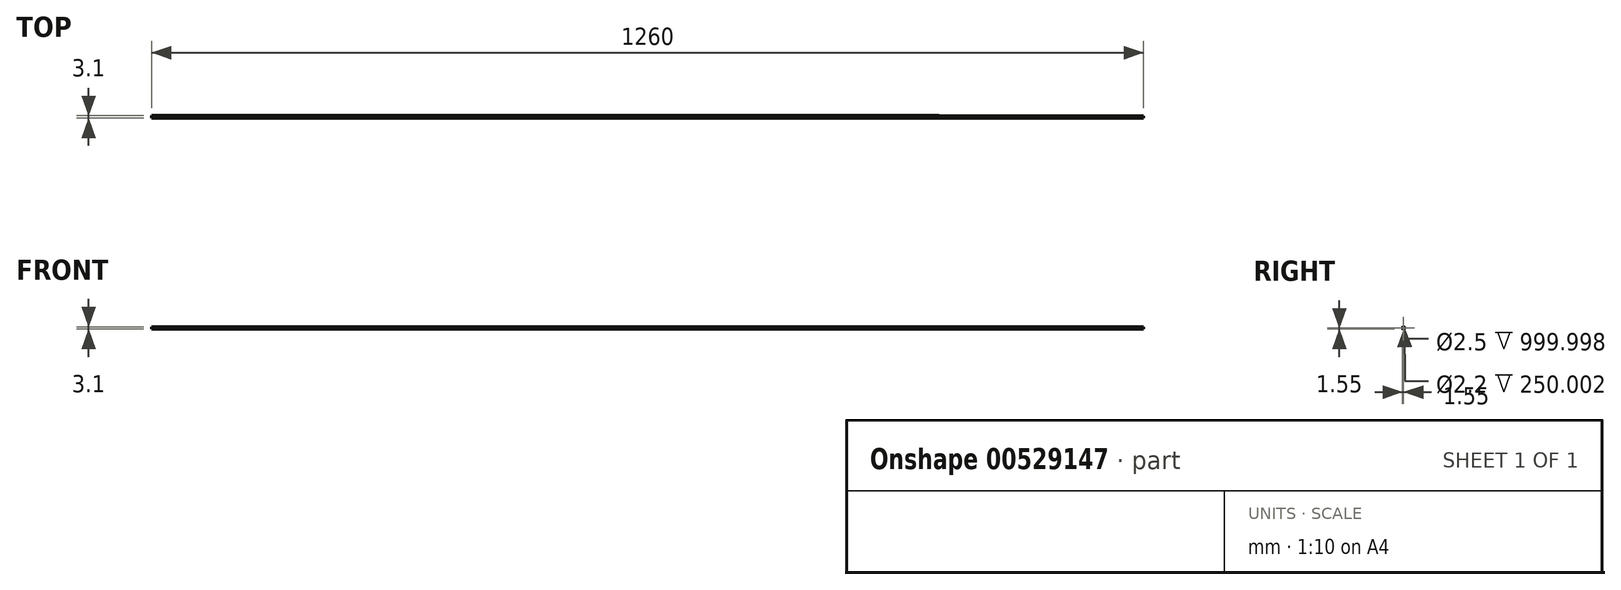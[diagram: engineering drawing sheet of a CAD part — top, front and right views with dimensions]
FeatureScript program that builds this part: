
annotation { "Feature Type Name" : "Feature", "Feature Type Description" : "" }
export const myFeature = defineFeature(function(context is Context, id is Id, definition is map)
    precondition{}
    {
        {
            var Q0;
            Q0=qCreatedBy(makeId("Front.planeOp"),FACE);
            var sketch = newSketch(context, id + "F0", { "sketchPlane" : qUnion([Q0])});
            skLineSegment(sketch, "E0", {"start": v(-197.41, 0) * mm, "end": v(187.07, 0) * mm});
            skLineSegment(sketch, "E1", {"start": v(-986.3, 1.55) * mm, "end": v(13.7, 1.55) * mm});
            skLineSegment(sketch, "E2", {"start": v(13.7, 1.55) * mm, "end": v(23.7, 1.4) * mm});
            skLineSegment(sketch, "E3", {"start": v(23.7, 1.4) * mm, "end": v(273.7, 1.4) * mm});
            skLineSegment(sketch, "E4.0", {"start": v(23.7, 1.1) * mm, "end": v(273.7, 1.1) * mm});
            skLineSegment(sketch, "E4.1", {"start": v(13.7, 1.25) * mm, "end": v(23.7, 1.1) * mm});
            skLineSegment(sketch, "E4.2", {"start": v(-986.3, 1.25) * mm, "end": v(13.7, 1.25) * mm});
            skLineSegment(sketch, "E5", {"start": v(273.7, 1.4) * mm, "end": v(273.7, 1.1) * mm});
            skLineSegment(sketch, "E6", {"start": v(-986.3, 1.55) * mm, "end": v(-986.3, 1.25) * mm});
            skSolve(sketch);
        }
        {
            var Q0;
            Q0 = qSketchRegion(id + "F0", true);
            var Q1;
            Q1=sQuery(id+"F0.wireOp",EDGE,"E0");
            revolve(context, id + "F1", {"entities" : qUnion([Q0]), "axis" : qUnion([Q1]), "revolveType" : RevolveType.FULL});
        }
    });
